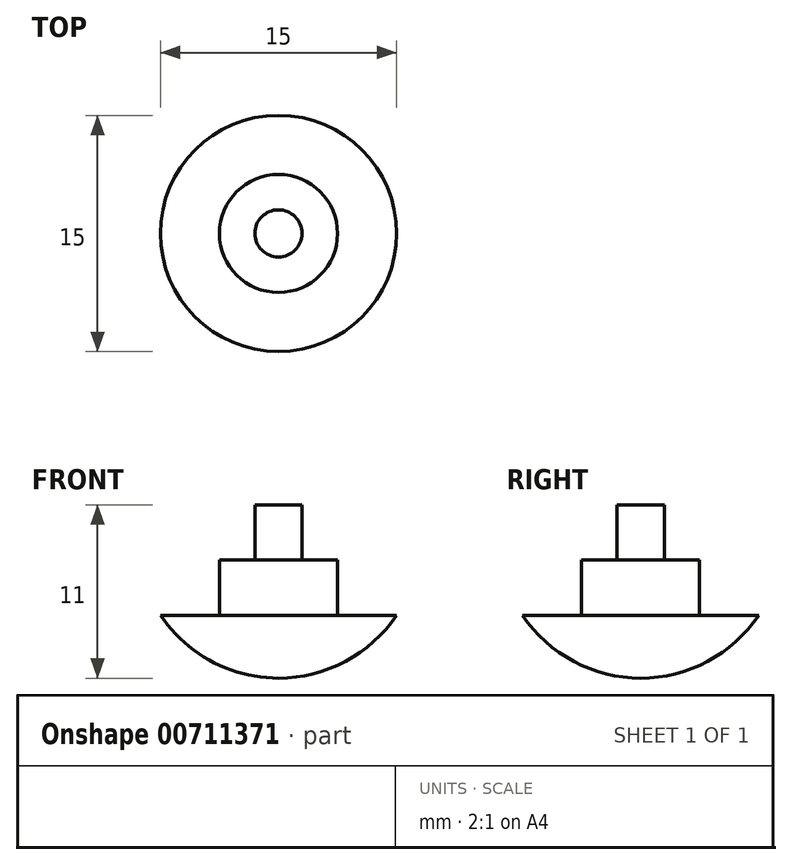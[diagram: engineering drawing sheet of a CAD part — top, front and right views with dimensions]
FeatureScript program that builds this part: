
annotation { "Feature Type Name" : "Feature", "Feature Type Description" : "" }
export const myFeature = defineFeature(function(context is Context, id is Id, definition is map)
    precondition{}
    {
        {
            var Q0;
            Q0=qCreatedBy(makeId("Front.planeOp"),FACE);
            var sketch = newSketch(context, id + "F0", { "sketchPlane" : qUnion([Q0])});
            skLineSegment(sketch, "E0", {"start": v(0, 0) * mm, "end": v(0, 11) * mm});
            skLineSegment(sketch, "E1", {"start": v(0, 11) * mm, "end": v(1.5, 11) * mm});
            skLineSegment(sketch, "E2", {"start": v(1.5, 11) * mm, "end": v(1.5, 7.5) * mm});
            skLineSegment(sketch, "E3", {"start": v(1.5, 7.5) * mm, "end": v(3.75, 7.5) * mm});
            skLineSegment(sketch, "E4", {"start": v(3.75, 7.5) * mm, "end": v(3.75, 4) * mm});
            skLineSegment(sketch, "E5", {"start": v(3.75, 4) * mm, "end": v(7.5, 4) * mm});
            skArc(sketch, "E6", {"start": v(0, 0) * mm, "mid": v(4.25, 1.06) * mm, "end": v(7.5, 4) * mm});
            skSolve(sketch);
        }
        {
            var Q0;
            Q0=makeQuery(id+"F0.imprint","IMPRINT",FACE,{"disambiguationData":[TD([[makeQuery(id+"F0.imprint","IMPRINT",EDGE,{"derivedFrom":sQuery(id+"F0.wireOp",EDGE,"E0")}),-1.0]])]});
            var Q1;
            Q1=sQuery(id+"F0.wireOp",EDGE,"E0");
            revolve(context, id + "F1", {"surfaceOperationType" : NewSurfaceOperationType.NEW, "entities" : qUnion([Q0]), "axis" : qUnion([Q1]), "revolveType" : RevolveType.FULL});
        }
    });
